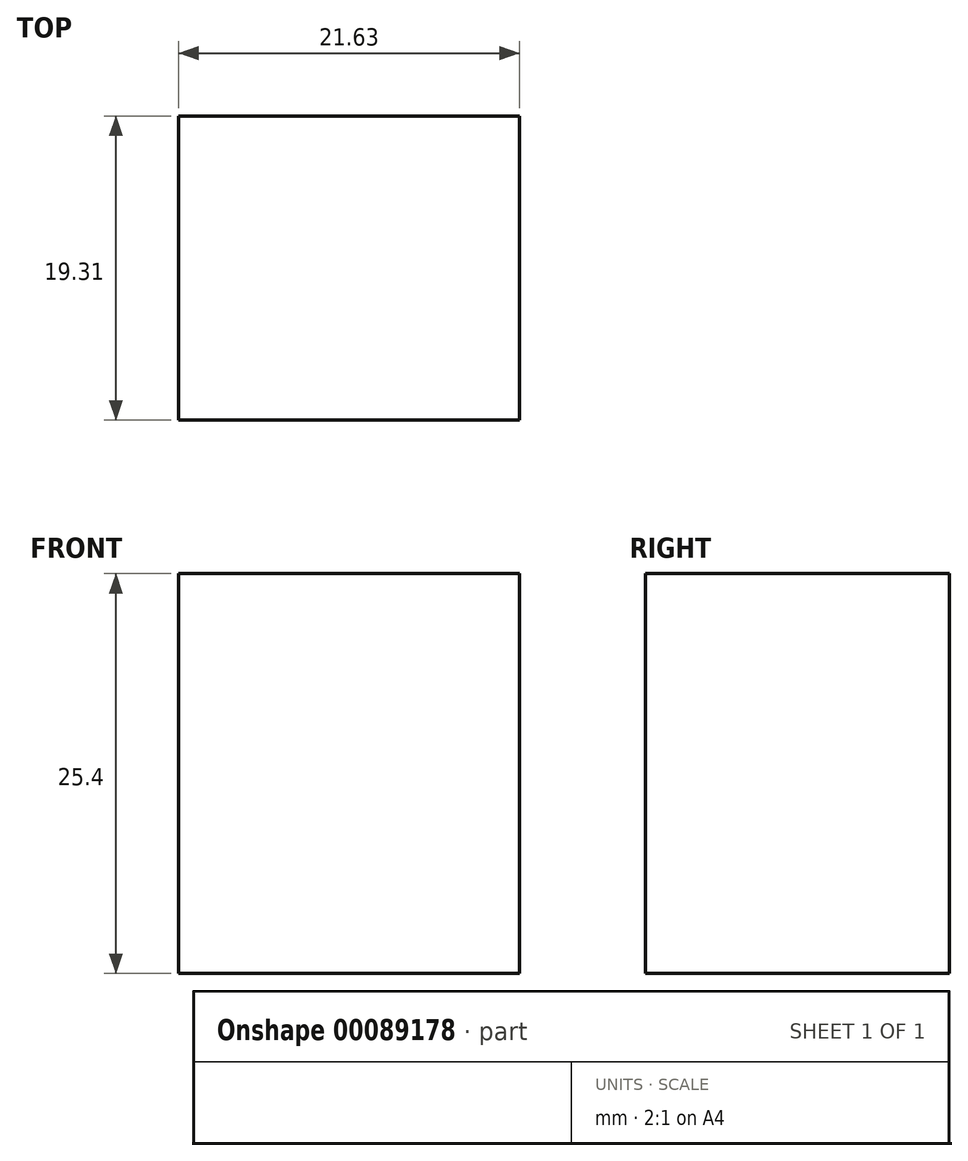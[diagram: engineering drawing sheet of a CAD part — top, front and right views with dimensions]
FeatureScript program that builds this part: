
annotation { "Feature Type Name" : "Feature", "Feature Type Description" : "" }
export const myFeature = defineFeature(function(context is Context, id is Id, definition is map)
    precondition{}
    {
        {
            var Q0;
            Q0=qCreatedBy(makeId("Top.planeOp"),FACE);
            var sketch = newSketch(context, id + "F0", { "sketchPlane" : qUnion([Q0])});
            skLineSegment(sketch, "E0.bottom", {"start": v(0, 0) * mm, "end": v(21.63, 0) * mm});
            skLineSegment(sketch, "E0.top", {"start": v(0, -19.31) * mm, "end": v(21.63, -19.31) * mm});
            skLineSegment(sketch, "E0.left", {"start": v(0, 0) * mm, "end": v(0, -19.31) * mm});
            skLineSegment(sketch, "E0.right", {"start": v(21.63, 0) * mm, "end": v(21.63, -19.31) * mm});
            skSolve(sketch);
        }
        {
            var Q0;
            Q0 = qSketchRegion(id + "F0", true);
            extrude(context, id + "F1", {"entities" : qUnion([Q0]), "depth" : 25.4 * mm});
        }
    });
